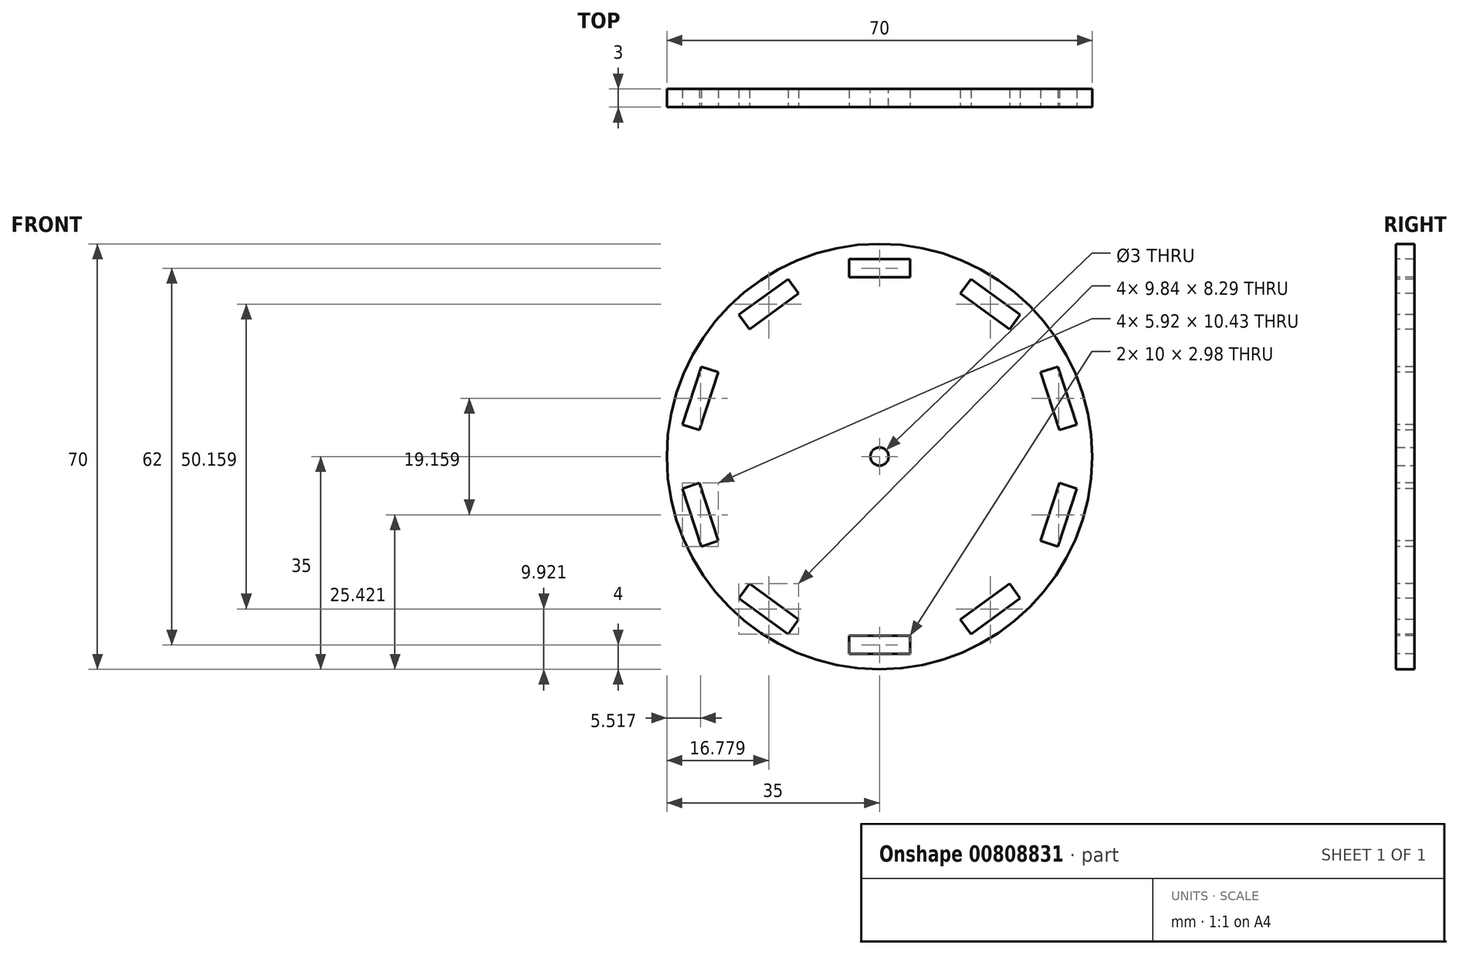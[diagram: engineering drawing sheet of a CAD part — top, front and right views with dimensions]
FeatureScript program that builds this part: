
annotation { "Feature Type Name" : "Feature", "Feature Type Description" : "" }
export const myFeature = defineFeature(function(context is Context, id is Id, definition is map)
    precondition{}
    {
        {
            var Q0;
            Q0=qCreatedBy(makeId("Front.planeOp"),FACE);
            var sketch = newSketch(context, id + "F0", { "sketchPlane" : qUnion([Q0])});
            skCircle(sketch, "E0", {"center": v(0, 0) * mm, "radius": 35 * mm});
            skCircle(sketch, "E1", {"center": v(0, 0) * mm, "radius": 1.5 * mm});
            skSolve(sketch);
        }
        {
            var Q0;
            Q0=qSketchRegion(id+"F0",true);
            extrude(context, id + "F1", {"entities" : qUnion([Q0]), "depth" : 3 * mm, "offsetDistance" : 25 * mm});
        }
        {
            var Q0;
            Q0=makeQuery(id+"F1.opExtrude","CAP_FACE",FACE,{"disambiguationData":[OSD([sQuery(id+"F0.wireOp",EDGE,"E0"),sQuery(id+"F0.wireOp",EDGE,"E1")])],"isStart":false});
            var sketch = newSketch(context, id + "F2", { "sketchPlane" : qUnion([Q0])});
            skLineSegment(sketch, "E2.bottom", {"start": v(5, -29.5) * mm, "end": v(-5, -29.5) * mm});
            skLineSegment(sketch, "E2.top", {"start": v(5, -32.49) * mm, "end": v(-5, -32.49) * mm});
            skLineSegment(sketch, "E2.left", {"start": v(5, -29.5) * mm, "end": v(5, -32.49) * mm});
            skLineSegment(sketch, "E2.right", {"start": v(-5, -29.5) * mm, "end": v(-5, -32.49) * mm});
            skPoint(sketch, "E2.middle", {"position": v(0, -31) * mm});
            skLineSegment(sketch, "E3.1.0", {"start": v(21.4, -20.94) * mm, "end": v(13.3, -26.81) * mm});
            skLineSegment(sketch, "E3.1.1", {"start": v(21.4, -20.94) * mm, "end": v(23.14, -23.35) * mm});
            skLineSegment(sketch, "E3.1.2", {"start": v(23.14, -23.35) * mm, "end": v(15.05, -29.22) * mm});
            skLineSegment(sketch, "E3.1.3", {"start": v(13.3, -26.81) * mm, "end": v(15.05, -29.22) * mm});
            skLineSegment(sketch, "E3.2.0", {"start": v(29.61, -4.36) * mm, "end": v(26.52, -13.87) * mm});
            skLineSegment(sketch, "E3.2.1", {"start": v(29.61, -4.36) * mm, "end": v(32.44, -5.28) * mm});
            skLineSegment(sketch, "E3.2.2", {"start": v(32.44, -5.28) * mm, "end": v(29.35, -14.8) * mm});
            skLineSegment(sketch, "E3.2.3", {"start": v(26.52, -13.87) * mm, "end": v(29.35, -14.8) * mm});
            skLineSegment(sketch, "E3.3.0", {"start": v(26.52, 13.87) * mm, "end": v(29.61, 4.36) * mm});
            skLineSegment(sketch, "E3.3.1", {"start": v(26.52, 13.87) * mm, "end": v(29.35, 14.8) * mm});
            skLineSegment(sketch, "E3.3.2", {"start": v(29.35, 14.8) * mm, "end": v(32.44, 5.28) * mm});
            skLineSegment(sketch, "E3.3.3", {"start": v(29.61, 4.36) * mm, "end": v(32.44, 5.28) * mm});
            skLineSegment(sketch, "E3.4.0", {"start": v(13.3, 26.81) * mm, "end": v(21.4, 20.94) * mm});
            skLineSegment(sketch, "E3.4.1", {"start": v(13.3, 26.81) * mm, "end": v(15.05, 29.22) * mm});
            skLineSegment(sketch, "E3.4.2", {"start": v(15.05, 29.22) * mm, "end": v(23.14, 23.35) * mm});
            skLineSegment(sketch, "E3.4.3", {"start": v(21.4, 20.94) * mm, "end": v(23.14, 23.35) * mm});
            skLineSegment(sketch, "E3.5.0", {"start": v(-5, 29.5) * mm, "end": v(5, 29.5) * mm});
            skLineSegment(sketch, "E3.5.1", {"start": v(-5, 29.5) * mm, "end": v(-5, 32.49) * mm});
            skLineSegment(sketch, "E3.5.2", {"start": v(-5, 32.49) * mm, "end": v(5, 32.49) * mm});
            skLineSegment(sketch, "E3.5.3", {"start": v(5, 29.5) * mm, "end": v(5, 32.49) * mm});
            skLineSegment(sketch, "E3.6.0", {"start": v(-21.4, 20.94) * mm, "end": v(-13.3, 26.81) * mm});
            skLineSegment(sketch, "E3.6.1", {"start": v(-21.4, 20.94) * mm, "end": v(-23.14, 23.35) * mm});
            skLineSegment(sketch, "E3.6.2", {"start": v(-23.14, 23.35) * mm, "end": v(-15.05, 29.22) * mm});
            skLineSegment(sketch, "E3.6.3", {"start": v(-13.3, 26.81) * mm, "end": v(-15.05, 29.22) * mm});
            skLineSegment(sketch, "E3.7.0", {"start": v(-29.61, 4.36) * mm, "end": v(-26.52, 13.87) * mm});
            skLineSegment(sketch, "E3.7.1", {"start": v(-29.61, 4.36) * mm, "end": v(-32.44, 5.28) * mm});
            skLineSegment(sketch, "E3.7.2", {"start": v(-32.44, 5.28) * mm, "end": v(-29.35, 14.8) * mm});
            skLineSegment(sketch, "E3.7.3", {"start": v(-26.52, 13.87) * mm, "end": v(-29.35, 14.8) * mm});
            skLineSegment(sketch, "E3.8.0", {"start": v(-26.52, -13.87) * mm, "end": v(-29.61, -4.36) * mm});
            skLineSegment(sketch, "E3.8.1", {"start": v(-26.52, -13.87) * mm, "end": v(-29.35, -14.8) * mm});
            skLineSegment(sketch, "E3.8.2", {"start": v(-29.35, -14.8) * mm, "end": v(-32.44, -5.28) * mm});
            skLineSegment(sketch, "E3.8.3", {"start": v(-29.61, -4.36) * mm, "end": v(-32.44, -5.28) * mm});
            skPoint(sketch, "E3.center", {"position": v(0, 0) * mm});
            skLineSegment(sketch, "E4.2.9.0", {"start": v(-13.3, -26.81) * mm, "end": v(-21.4, -20.94) * mm});
            skLineSegment(sketch, "E4.3.9.0", {"start": v(-13.3, -26.81) * mm, "end": v(-15.05, -29.22) * mm});
            skLineSegment(sketch, "E4.6.9.0", {"start": v(-15.05, -29.22) * mm, "end": v(-23.14, -23.35) * mm});
            skLineSegment(sketch, "E4.9.9.0", {"start": v(-21.4, -20.94) * mm, "end": v(-23.14, -23.35) * mm});
            skSolve(sketch);
        }
        {
            var Q0;
            Q0=qSketchRegion(id+"F2",true);
            extrude(context, id + "F3", {"entities" : qUnion([Q0]), "operationType" : NewBodyOperationType.REMOVE, "oppositeDirection" : true, "depth" : 25 * mm, "offsetDistance" : 25 * mm});
        }
    });
